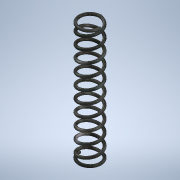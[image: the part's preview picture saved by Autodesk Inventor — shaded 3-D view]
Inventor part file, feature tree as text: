
AUTODESK INVENTOR PART (.ipt)
format: ipt  version: 2020.1 (Build 241239000, 239)  size: 310,272 bytes
history: native  units: mm
features: sketch x3, revolve x2, projected_geometry x2, helix x1
ambient origin geometry x8: Origin, YZ Plane, XZ Plane, XY Plane, X Axis, Y Axis, Z Axis, Center Point
bodies: Solid1 (feature_tree)
feature tree (8):
  helix  "Coil1"  [1 undecoded]
  revolve  "Revolution1"  [1 undecoded]
  revolve  "Revolution2"  Angle=270.0deg
  sketch  "Sketch1"  dims[d1=0.32mm d2=1.2mm]
  sketch  "Sketch2"  dims[d3=1.356mm]
  projected_geometry  "Projected Loop1"
  sketch  "Sketch3"  dims[d4=10.0mm d5=100.0mm d6=0.0mm d7=90.0deg d8=90.0deg d9=0.0mm d10=0.0mm d11=270.0deg d12=270.0deg]
  projected_geometry  "Projected Loop2"
note: 2 required parameter values undecoded (feature->parameter linkage not recoverable at this tier; creation-order binding heuristic only, values carry confidence <= 0.55)